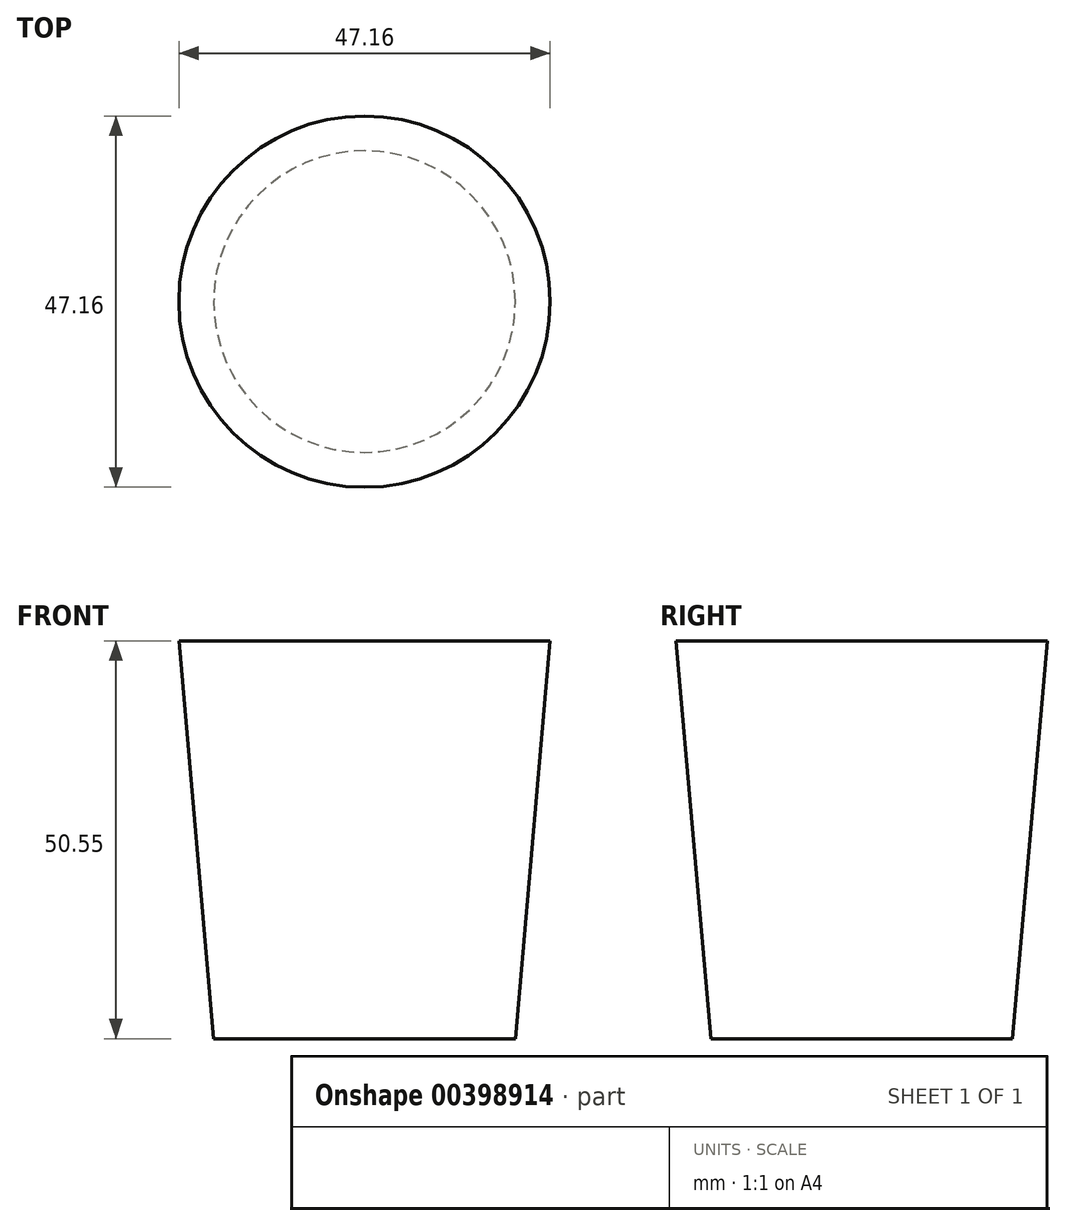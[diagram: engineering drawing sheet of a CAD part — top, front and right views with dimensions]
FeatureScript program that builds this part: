
annotation { "Feature Type Name" : "Feature", "Feature Type Description" : "" }
export const myFeature = defineFeature(function(context is Context, id is Id, definition is map)
    precondition{}
    {
        {
            var Q0;
            Q0=qCreatedBy(makeId("Top.planeOp"),FACE);
            var sketch = newSketch(context, id + "F0", { "sketchPlane" : qUnion([Q0])});
            skCircle(sketch, "E0", {"center": v(0, 0) * mm, "radius": 19.16 * mm});
            skSolve(sketch);
        }
        {
            var Q0;
            Q0=makeQuery(id+"F0.imprint","IMPRINT",FACE,{"disambiguationData":[TD([[makeQuery(id+"F0.imprint","IMPRINT",EDGE,{"derivedFrom":sQuery(id+"F0.wireOp",EDGE,"E0")}),1.0]])]});
            extrude(context, id + "F1", {"entities" : qUnion([Q0]), "depth" : 50.55 * mm, "hasDraft" : true, "draftAngle" : 5 * degree});
        }
    });
